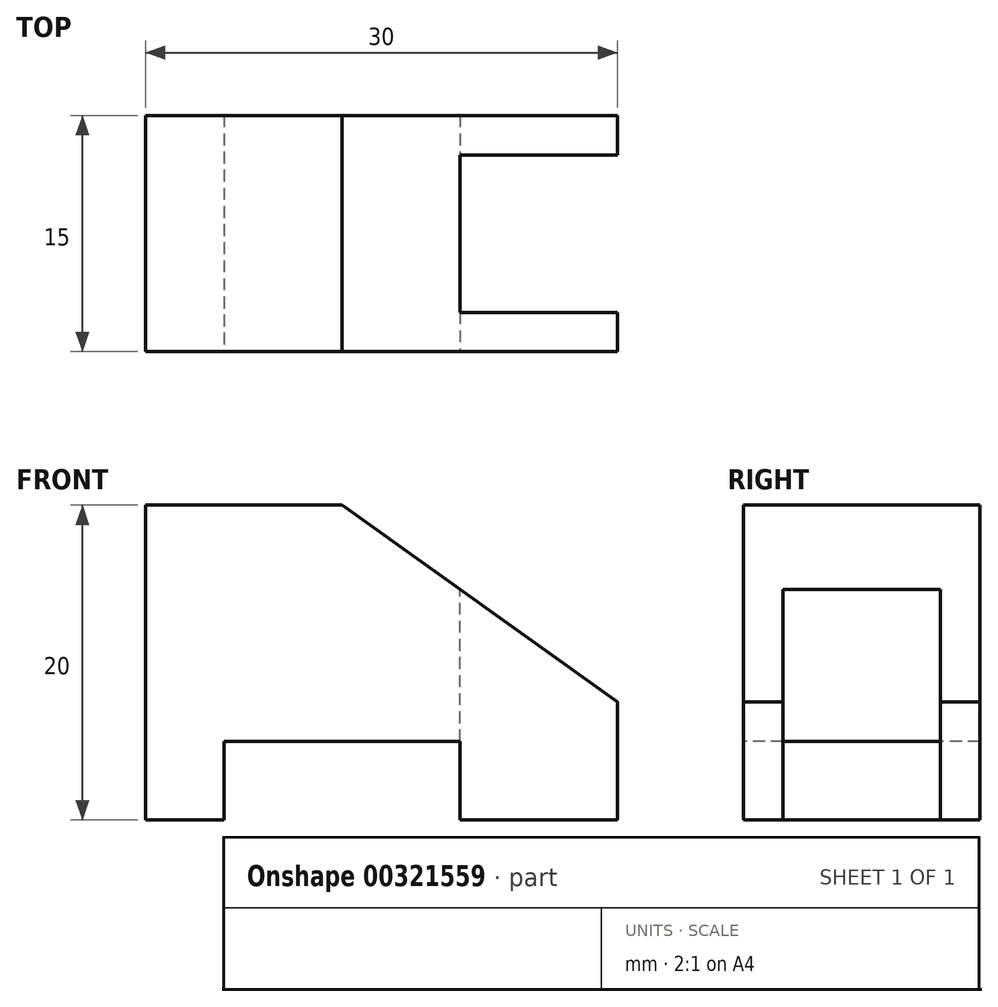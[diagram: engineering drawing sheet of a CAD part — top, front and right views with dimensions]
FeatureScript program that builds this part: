
annotation { "Feature Type Name" : "Feature", "Feature Type Description" : "" }
export const myFeature = defineFeature(function(context is Context, id is Id, definition is map)
    precondition{}
    {
        {
            var Q0;
            Q0=qCreatedBy(makeId("Front.planeOp"),FACE);
            var sketch = newSketch(context, id + "F0", { "sketchPlane" : qUnion([Q0])});
            skLineSegment(sketch, "E0", {"start": v(0, 0) * mm, "end": v(0, 20) * mm});
            skLineSegment(sketch, "E1", {"start": v(0, 20) * mm, "end": v(12.5, 20) * mm});
            skLineSegment(sketch, "E2", {"start": v(12.5, 20) * mm, "end": v(30, 7.5) * mm});
            skLineSegment(sketch, "E3", {"start": v(30, 7.5) * mm, "end": v(30, 0) * mm});
            skLineSegment(sketch, "E4", {"start": v(30, 0) * mm, "end": v(0, 0) * mm});
            skSolve(sketch);
        }
        {
            var Q0;
            Q0 = qSketchRegion(id + "F0", true);
            extrude(context, id + "F1", {"entities" : qUnion([Q0]), "depth" : 15 * mm});
        }
        {
            var Q0;
            Q0=makeQuery(id+"F1.opExtrude","CAP_FACE",FACE,{"disambiguationData":[OSD([sQuery(id+"F0.wireOp",EDGE,"E0"),sQuery(id+"F0.wireOp",EDGE,"E1"),sQuery(id+"F0.wireOp",EDGE,"E2"),sQuery(id+"F0.wireOp",EDGE,"E3"),sQuery(id+"F0.wireOp",EDGE,"E4")])],"isStart":false});
            var sketch = newSketch(context, id + "F2", { "sketchPlane" : qUnion([Q0])});
            skLineSegment(sketch, "E5", {"start": v(5, 0) * mm, "end": v(5, 5) * mm});
            skLineSegment(sketch, "E6", {"start": v(5, 5) * mm, "end": v(20, 5) * mm});
            skLineSegment(sketch, "E7", {"start": v(20, 5) * mm, "end": v(20, 0) * mm});
            skLineSegment(sketch, "E8", {"start": v(20, 0) * mm, "end": v(5, 0) * mm});
            skSolve(sketch);
        }
        {
            var Q0;
            Q0 = qSketchRegion(id + "F2", true);
            extrude(context, id + "F3", {"entities" : qUnion([Q0]), "operationType" : NewBodyOperationType.REMOVE, "endBound" : BoundingType.THROUGH_ALL, "oppositeDirection" : true, "depth" : 25 * mm});
        }
        {
            var Q0;
            Q0=makeQuery(id+"F1.opExtrude","SWEPT_FACE",FACE,{"disambiguationData":[OSD([sQuery(id+"F0.wireOp",EDGE,"E3")])]});
            var sketch = newSketch(context, id + "F4", { "sketchPlane" : qUnion([Q0])});
            skLineSegment(sketch, "E9", {"start": v(-12.5, 0) * mm, "end": v(-12.5, 15) * mm});
            skLineSegment(sketch, "E10", {"start": v(-12.5, 15) * mm, "end": v(-2.5, 15) * mm});
            skLineSegment(sketch, "E11", {"start": v(-2.5, 15) * mm, "end": v(-2.5, 0) * mm});
            skLineSegment(sketch, "E12", {"start": v(-2.5, 0) * mm, "end": v(-12.5, 0) * mm});
            skSolve(sketch);
        }
        {
            var Q0;
            Q0 = qSketchRegion(id + "F4", true);
            extrude(context, id + "F5", {"entities" : qUnion([Q0]), "operationType" : NewBodyOperationType.REMOVE, "oppositeDirection" : true, "depth" : 10 * mm});
        }
    });
